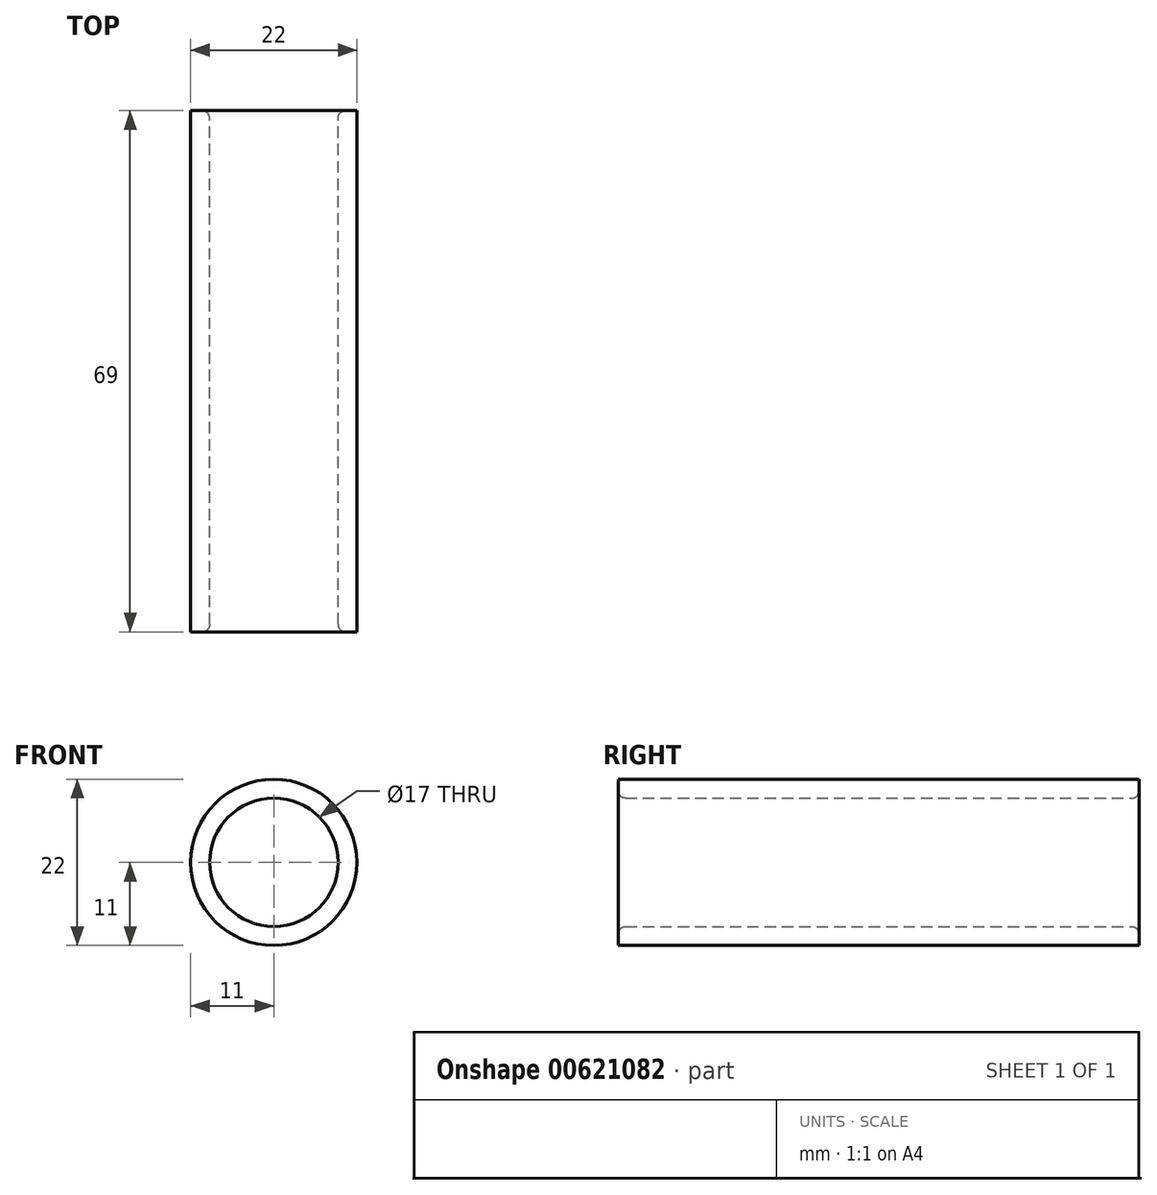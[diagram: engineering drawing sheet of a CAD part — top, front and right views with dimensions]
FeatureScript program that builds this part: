
annotation { "Feature Type Name" : "Feature", "Feature Type Description" : "" }
export const myFeature = defineFeature(function(context is Context, id is Id, definition is map)
    precondition{}
    {
        {
            var Q0;
            Q0=qCreatedBy(makeId("Front.planeOp"),FACE);
            var sketch = newSketch(context, id + "F0", { "sketchPlane" : qUnion([Q0])});
            skCircle(sketch, "E0", {"center": v(0, 0) * mm, "radius": 8.5 * mm});
            skCircle(sketch, "E1", {"center": v(0, 0) * mm, "radius": 11 * mm});
            skSolve(sketch);
        }
        {
            var Q0;
            Q0 = qSketchRegion(id + "F0", true);
            extrude(context, id + "F1", {"entities" : qUnion([Q0]), "endBound" : BoundingType.SYMMETRIC, "depth" : 69 * mm, "offsetDistance" : 25 * mm});
        }
        {
            var Q0;
            Q0=makeQuery(id+"F1.opExtrude","CAP_EDGE",EDGE,{"disambiguationData":[OSD([sQuery(id+"F0.wireOp",EDGE,"E0")])],"isStart":false});
            var Q1;
            Q1=makeQuery(id+"F1.opExtrude","CAP_EDGE",EDGE,{"disambiguationData":[OSD([sQuery(id+"F0.wireOp",EDGE,"E0")])],"isStart":true});
            fillet(context, id + "F2", {"entities" : qUnion([Q0, Q1]), "radius" : 1 * mm, "tangentPropagation" : true, "allowEdgeOverflow" : false});
        }
    });
